# Revit family: Hekatron_Feststellanlagen_THM 425-1_DE_22.01
name_source: partatom
category: Brandmelder
revit_build: Autodesk Revit 2018 (Build: 20190510_1515(x64)
units: mm (PartAtom-declared; Revit-internal decimal feet)

## family parameters
Basisbauteil = Fläche
Beim Laden mit Abzugskörper schneiden = Nein
Bemaßung runder Anschluss = Durchmesser verwenden
Beschriftungsausrichtung beibehalten = Nein
Gemeinsam genutzt = Nein
Raumberechnungspunkt = Nein
Teiletyp = Normal

## types (1)
- THM 425-1
    Bauartgenehmigungen = Z-6.500-2405, Z-6.500-2325, Z-6.500-2359, Z-6.500-2393, Z-6.500-2394, Z-6.500-2414, Z-6.500-2415, Z-6.500-2407, Z-6.500-2365, Z-6.500-2403, Z-6.500-2419, Z-6.500-2298, Z-6.500-2442, Z-6.500-2444, Z-6.500-2451, Z-6.500-2452, Z-6.500-2454, Z-6.500-2459, Z-6.500-2499, Z-6.500-2515
    Beschreibung = Türhaftmagnet in runder Bauform mit verdeckten Anschlussklemmen. Mit Verpolschutz und Löschdiode. Passend zur Ankerplatte ASS 75.
    Betriebsspannung = 24 V DC
    Breite (mm) = 43.0
    EG-Konformitätszertifikat / Zertifikat der Leistungsbeständigkeit = 0786-CPR-21370
    Farbe = Metall / Schwarz
    Hersteller = Hekatron
    Höhe (mm) = 97.0
    Kabeleinführung = unten
    Leistungserklärung (DoP) = CPR-31-13-501-de-en
    Link zu Ausschreibungstext = https://www.meinhplus.de
    Link zu Produktinformation = https://www.hekatron-planungstools.de
    Link zu ausschreiben.de = http://www.ausschreiben.de
    Material = Metall
    Modell = THM 425-1
    Montageart = Aufputz
    Schutzart = IP 40
    Stromaufnahme = max. 63mA
    Tiefe (mm) = 75.0
    Typenkommentare = Türhaftmagnet THM 425-1
    UB A&S Artikel Nummer = 6500020
    URL = https://www.hekatron-brandschutz.de
    Version des BIM Objektes = 22.01
    Vorgabe-Ansicht = 1200 mm
    Zulässige Umgebungstemperatur = 0 °C bis +50 °C

## geometry (parser evidence)
native form markers: Sweep x1
no freeform markers — native parametric forms only
